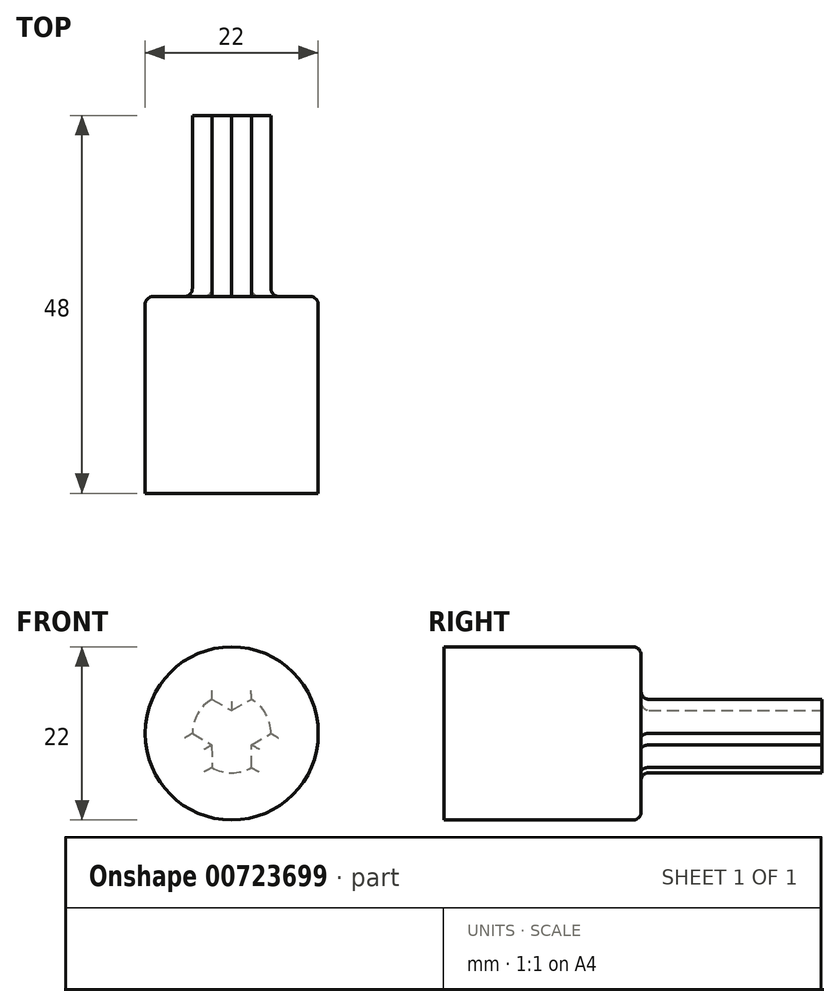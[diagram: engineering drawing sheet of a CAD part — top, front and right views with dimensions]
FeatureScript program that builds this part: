
annotation { "Feature Type Name" : "Feature", "Feature Type Description" : "" }
export const myFeature = defineFeature(function(context is Context, id is Id, definition is map)
    precondition{}
    {
        {
            var Q0;
            Q0=qCreatedBy(makeId("Front.planeOp"),FACE);
            var sketch = newSketch(context, id + "F0", { "sketchPlane" : qUnion([Q0])});
            skCircle(sketch, "E0.cCircle", {"center": v(0, 0) * mm, "radius": 5 * mm});
            skLineSegment(sketch, "E0.0", {"start": v(-5, 0) * mm, "end": v(-2.5, 4.33) * mm});
            skLineSegment(sketch, "E0.1", {"start": v(-2.5, 4.33) * mm, "end": v(2.5, 4.33) * mm});
            skLineSegment(sketch, "E0.2", {"start": v(2.5, 4.33) * mm, "end": v(5, 0) * mm});
            skLineSegment(sketch, "E0.3", {"start": v(5, 0) * mm, "end": v(2.5, -4.33) * mm});
            skLineSegment(sketch, "E0.4", {"start": v(2.5, -4.33) * mm, "end": v(-2.5, -4.33) * mm});
            skLineSegment(sketch, "E0.5", {"start": v(-2.5, -4.33) * mm, "end": v(-5, 0) * mm});
            skLineSegment(sketch, "E1", {"start": v(-2.5, 4.33) * mm, "end": v(0, 2.92) * mm});
            skLineSegment(sketch, "E2", {"start": v(0, 2.92) * mm, "end": v(2.5, 4.33) * mm});
            skLineSegment(sketch, "E3", {"start": v(-5, 0) * mm, "end": v(-2.53, -1.46) * mm});
            skLineSegment(sketch, "E4", {"start": v(-2.53, -1.46) * mm, "end": v(-2.5, -4.33) * mm});
            skLineSegment(sketch, "E5", {"start": v(2.5, -4.33) * mm, "end": v(2.53, -1.46) * mm});
            skLineSegment(sketch, "E6", {"start": v(2.53, -1.46) * mm, "end": v(5, 0) * mm});
            skSolve(sketch);
        }
        {
            var Q0;
            Q0=makeQuery(id+"F0.imprint","IMPRINT",FACE,{"disambiguationData":[TD([[makeQuery(id+"F0.imprint","IMPRINT",EDGE,{"derivedFrom":sQuery(id+"F0.wireOp",EDGE,"E0.0")}),-1.0]])]});
            extrude(context, id + "F1", {"entities" : qUnion([Q0]), "depth" : 23 * mm, "offsetDistance" : 25 * mm});
        }
        {
            var Q0;
            {var subQ0=sQuery(id+"F0.wireOp",EDGE,"E0.2");Q0=makeQuery(id+"F0.imprint","IMPRINT",FACE,{"disambiguationData":[TD([[makeQuery(id+"F0.imprint","IMPRINT",EDGE,{"derivedFrom":subQ0}),1.0]])]});}
            var Q1;
            {var subQ0=sQuery(id+"F0.wireOp",EDGE,"E0.0");Q1=makeQuery(id+"F0.imprint","IMPRINT",FACE,{"disambiguationData":[TD([[makeQuery(id+"F0.imprint","IMPRINT",EDGE,{"derivedFrom":subQ0}),1.0]])]});}
            var Q2;
            {var subQ0=sQuery(id+"F0.wireOp",EDGE,"E0.4");Q2=makeQuery(id+"F0.imprint","IMPRINT",FACE,{"disambiguationData":[TD([[makeQuery(id+"F0.imprint","IMPRINT",EDGE,{"derivedFrom":subQ0}),1.0]])]});}
            var Q3;
            Q3=makeQuery(id+"F1.opExtrude","CAP_VERTEX",VERTEX,{"disambiguationData":[OSD([sQuery(id+"F0.wireOp",EDGE,"E0.cCircle"),sQuery(id+"F0.wireOp",EDGE,"E0.0"),sQuery(id+"F0.wireOp",EDGE,"E0.1"),sQuery(id+"F0.wireOp",EDGE,"E1")])],"isStart":false});
            extrude(context, id + "F2", {"entities" : qUnion([Q0, Q1, Q2]), "operationType" : NewBodyOperationType.ADD, "endBound" : BoundingType.UP_TO_VERTEX, "depth" : 25 * mm, "endBoundEntityVertex" : qUnion([Q3]), "offsetDistance" : 25 * mm});
        }
        {
            var Q0;
            {var subQ0=dummyQuery(id+"F2.vertexPlane.planeOp",FACE);Q0=makeQuery(id+"F2.boolean.opBoolean","MERGE",FACE,{"derivedFrom":[makeQuery(id+"F1.opExtrude","CAP_FACE",FACE,{"disambiguationData":[OSD([sQuery(id+"F0.wireOp",EDGE,"E0.0"),sQuery(id+"F0.wireOp",EDGE,"E0.2"),sQuery(id+"F0.wireOp",EDGE,"E0.4"),sQuery(id+"F0.wireOp",EDGE,"E1"),sQuery(id+"F0.wireOp",EDGE,"E2"),sQuery(id+"F0.wireOp",EDGE,"E3"),sQuery(id+"F0.wireOp",EDGE,"E4"),sQuery(id+"F0.wireOp",EDGE,"E5"),sQuery(id+"F0.wireOp",EDGE,"E6")])],"isStart":false}),makeQuery(id+"F2.opExtrude","CAP_FACE",FACE,{"disambiguationData":[OSD([subQ0]),OD(0.0)],"isStart":false}),makeQuery(id+"F2.opExtrude","CAP_FACE",FACE,{"disambiguationData":[OSD([subQ0]),OD(1.0)],"isStart":false}),makeQuery(id+"F2.opExtrude","CAP_FACE",FACE,{"disambiguationData":[OSD([subQ0]),OD(2.0)],"isStart":false})]});}
            var sketch = newSketch(context, id + "F3", { "sketchPlane" : qUnion([Q0])});
            skCircle(sketch, "E7", {"center": v(0, 0) * mm, "radius": 11 * mm});
            skSolve(sketch);
        }
        {
            var Q0;
            Q0=makeQuery(id+"F3.imprint","IMPRINT",FACE,{"disambiguationData":[TD([[makeQuery(id+"F3.imprint","IMPRINT",EDGE,{"derivedFrom":sQuery(id+"F3.wireOp",EDGE,"E7")}),1.0]])]});
            var Q1;
            {var subQ3=sQuery(id+"F0.wireOp",EDGE,"E1");Q1=makeQuery(id+"F3.imprint","IMPRINT",FACE,{"disambiguationData":[TD([[makeQuery(id+"F3.imprint","IMPRINT",EDGE,{"derivedFrom":makeQuery(id+"F1.opExtrude","CAP_EDGE",EDGE,{"disambiguationData":[OSD([subQ3])],"isStart":false})}),-1.0]])]});}
            extrude(context, id + "F4", {"entities" : qUnion([Q0, Q1]), "operationType" : NewBodyOperationType.ADD, "depth" : 25 * mm, "offsetDistance" : 25 * mm});
        }
        {
            var Q0;
            Q0=makeQuery(id+"F4.opExtrude","CAP_FACE",FACE,{"disambiguationData":[OSD([sQuery(id+"F3.wireOp",EDGE,"E7")])],"isStart":true});
            fillet(context, id + "F5", {"entities" : qUnion([Q0]), "radius" : 1 * mm, "tangentPropagation" : true, "allowEdgeOverflow" : false});
        }
    });
